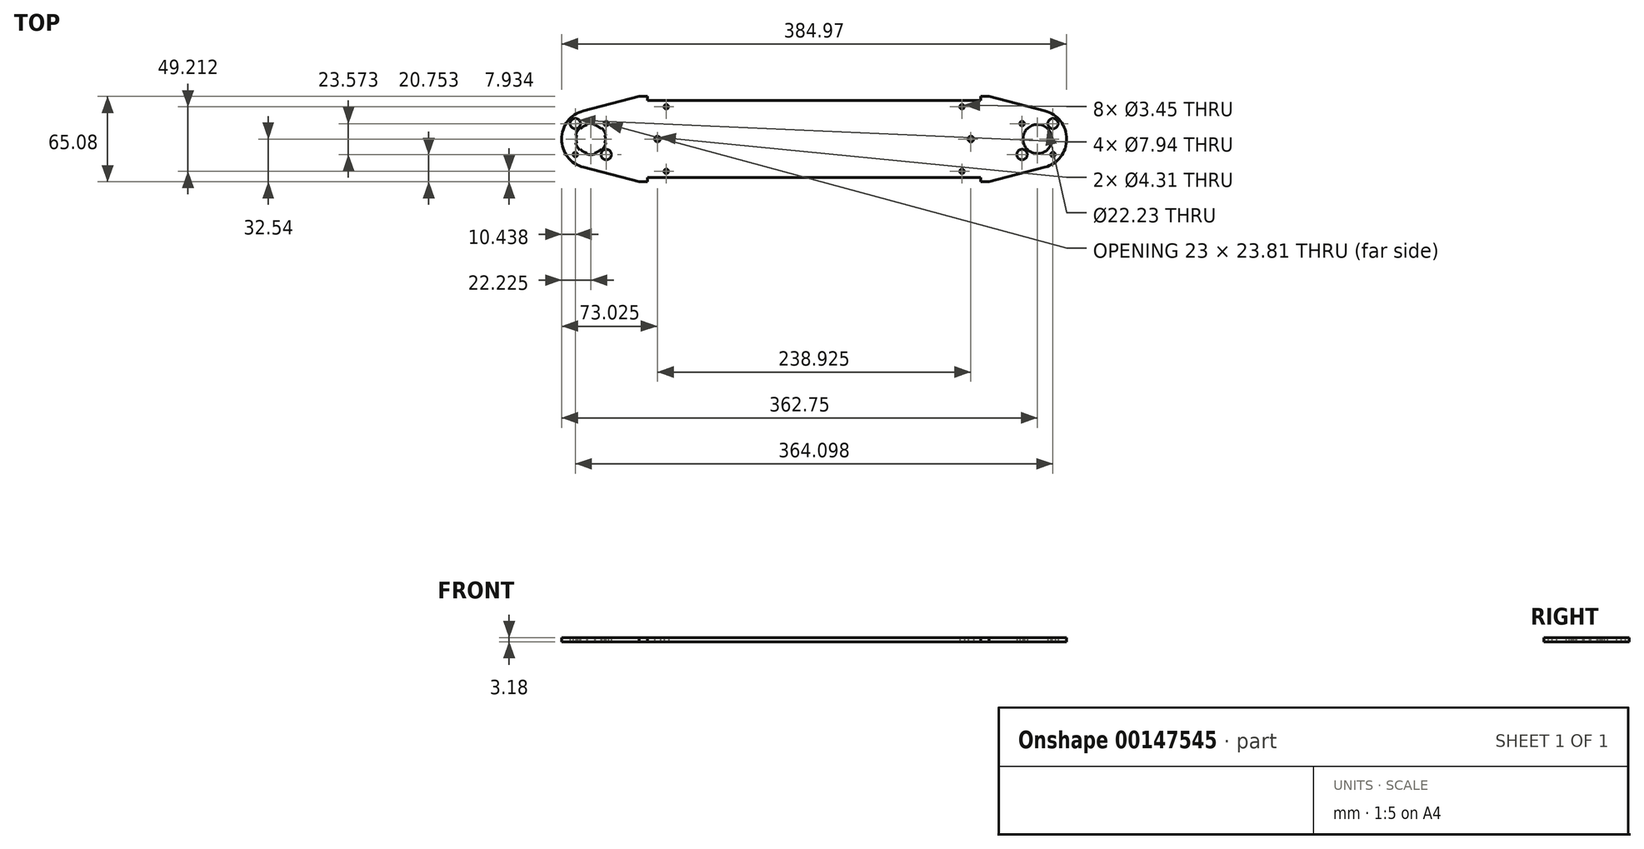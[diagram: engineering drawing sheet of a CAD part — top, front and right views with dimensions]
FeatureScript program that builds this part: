
annotation { "Feature Type Name" : "Feature", "Feature Type Description" : "" }
export const myFeature = defineFeature(function(context is Context, id is Id, definition is map)
    precondition{}
    {
        {
            var Q0;
            Q0=qCreatedBy(makeId("Top.planeOp"),FACE);
            var sketch = newSketch(context, id + "F0", { "sketchPlane" : qUnion([Q0])});
            skPoint(sketch, "E0.rect.middle", {"position": v(0, 0) * mm});
            skCircle(sketch, "E1", {"center": v(0, 0) * mm, "radius": 11.11 * mm});
            skLineSegment(sketch, "E2.bottom", {"start": v(11.79, 11.79) * mm, "end": v(-11.79, 11.79) * mm, "construction": true});
            skLineSegment(sketch, "E2.left", {"start": v(11.79, 11.79) * mm, "end": v(11.79, -11.79) * mm, "construction": true});
            skLineSegment(sketch, "E2.right", {"start": v(-11.79, 11.79) * mm, "end": v(-11.79, -11.79) * mm, "construction": true});
            skCircle(sketch, "E3", {"center": v(11.79, 11.79) * mm, "radius": 5.56 * mm, "construction": true});
            skCircle(sketch, "E4", {"center": v(-11.79, 11.79) * mm, "radius": 1.73 * mm});
            skCircle(sketch, "E5", {"center": v(11.79, 11.79) * mm, "radius": 3.97 * mm});
            skCircle(sketch, "E6", {"center": v(11.79, -11.79) * mm, "radius": 1.73 * mm});
            skCircle(sketch, "E7", {"center": v(-11.79, -11.79) * mm, "radius": 3.97 * mm});
            skArc(sketch, "E8", {"start": v(-346.1, 21.51) * mm, "mid": v(-362.75, 0) * mm, "end": v(-346.1, -21.51) * mm});
            skLineSegment(sketch, "E9.bottom", {"start": v(-352.31, 11.79) * mm, "end": v(-328.74, 11.79) * mm, "construction": true});
            skLineSegment(sketch, "E9.top", {"start": v(-352.31, -11.79) * mm, "end": v(-328.74, -11.79) * mm, "construction": true});
            skLineSegment(sketch, "E9.left", {"start": v(-352.31, 11.79) * mm, "end": v(-352.31, -11.79) * mm, "construction": true});
            skLineSegment(sketch, "E9.right", {"start": v(-328.74, 11.79) * mm, "end": v(-328.74, -11.79) * mm, "construction": true});
            skCircle(sketch, "E10", {"center": v(-328.74, 11.79) * mm, "radius": 1.73 * mm});
            skCircle(sketch, "E11", {"center": v(-340.53, 0) * mm, "radius": 11.11 * mm});
            skCircle(sketch, "E12", {"center": v(-352.31, 11.79) * mm, "radius": 3.97 * mm});
            skCircle(sketch, "E13", {"center": v(-352.31, -11.79) * mm, "radius": 1.73 * mm});
            skCircle(sketch, "E14", {"center": v(-328.74, -11.79) * mm, "radius": 3.97 * mm});
            skLineSegment(sketch, "E15", {"start": v(0, 0) * mm, "end": v(-340.53, 0) * mm, "construction": true});
            skLineSegment(sketch, "E16", {"start": v(-346.1, -21.51) * mm, "end": v(-303.61, -32.54) * mm});
            skLineSegment(sketch, "E17", {"start": v(-346.1, 21.51) * mm, "end": v(-303.61, 32.54) * mm});
            skLineSegment(sketch, "E18", {"start": v(-297.26, -29.37) * mm, "end": v(-43.26, -29.37) * mm});
            skLineSegment(sketch, "E19", {"start": v(-297.26, 29.37) * mm, "end": v(-43.26, 29.37) * mm});
            skLineSegment(sketch, "E20", {"start": v(-297.26, 32.54) * mm, "end": v(-297.26, 29.37) * mm});
            skLineSegment(sketch, "E21", {"start": v(-297.26, 32.54) * mm, "end": v(-303.61, 32.54) * mm});
            skLineSegment(sketch, "E22", {"start": v(-297.26, -29.37) * mm, "end": v(-297.26, -32.54) * mm});
            skLineSegment(sketch, "E23", {"start": v(-297.26, -32.54) * mm, "end": v(-303.61, -32.54) * mm});
            skLineSegment(sketch, "E24", {"start": v(-43.26, -29.37) * mm, "end": v(-43.26, -32.54) * mm});
            skLineSegment(sketch, "E25", {"start": v(-43.26, -32.54) * mm, "end": v(-36.91, -32.54) * mm});
            skLineSegment(sketch, "E26", {"start": v(-43.26, 29.37) * mm, "end": v(-43.26, 32.54) * mm});
            skLineSegment(sketch, "E27", {"start": v(-43.26, 32.54) * mm, "end": v(-36.91, 32.54) * mm});
            skLineSegment(sketch, "E28", {"start": v(-36.91, -32.54) * mm, "end": v(5.58, -21.51) * mm});
            skLineSegment(sketch, "E29", {"start": v(5.58, 21.51) * mm, "end": v(-36.91, 32.54) * mm});
            skArc(sketch, "E30", {"start": v(5.58, -21.51) * mm, "mid": v(22.23, 0) * mm, "end": v(5.58, 21.51) * mm});
            skLineSegment(sketch, "E31", {"start": v(-297.26, 29.37) * mm, "end": v(-297.26, 24.6) * mm, "construction": true});
            skLineSegment(sketch, "E32", {"start": v(-297.26, 24.6) * mm, "end": v(-282.98, 24.6) * mm, "construction": true});
            skLineSegment(sketch, "E33", {"start": v(-297.26, -29.37) * mm, "end": v(-297.26, -24.6) * mm, "construction": true});
            skLineSegment(sketch, "E34", {"start": v(-297.26, -24.6) * mm, "end": v(-282.98, -24.6) * mm, "construction": true});
            skLineSegment(sketch, "E35", {"start": v(-43.26, -29.37) * mm, "end": v(-43.26, -24.6) * mm, "construction": true});
            skLineSegment(sketch, "E36", {"start": v(-43.26, -24.6) * mm, "end": v(-57.55, -24.6) * mm, "construction": true});
            skLineSegment(sketch, "E37", {"start": v(-43.26, 29.37) * mm, "end": v(-43.26, 24.6) * mm, "construction": true});
            skLineSegment(sketch, "E38", {"start": v(-43.26, 24.6) * mm, "end": v(-57.55, 24.6) * mm, "construction": true});
            skCircle(sketch, "E39", {"center": v(-282.98, 24.6) * mm, "radius": 1.73 * mm});
            skCircle(sketch, "E40", {"center": v(-57.55, 24.6) * mm, "radius": 1.73 * mm});
            skCircle(sketch, "E41", {"center": v(-57.55, -24.6) * mm, "radius": 1.73 * mm});
            skCircle(sketch, "E42", {"center": v(-282.98, -24.6) * mm, "radius": 1.73 * mm});
            skLineSegment(sketch, "E43", {"start": v(-11.79, -11.79) * mm, "end": v(11.79, -11.79) * mm, "construction": true});
            skLineSegment(sketch, "E44", {"start": v(-170.26, -29.37) * mm, "end": v(-170.26, 0) * mm, "construction": true});
            skLineSegment(sketch, "E45", {"start": v(-170.26, 0) * mm, "end": v(-170.26, 29.37) * mm, "construction": true});
            skLineSegment(sketch, "E46", {"start": v(-328.74, 11.79) * mm, "end": v(-289.73, 11.79) * mm, "construction": true});
            skLineSegment(sketch, "E47", {"start": v(-289.73, 11.79) * mm, "end": v(-289.73, 0) * mm, "construction": true});
            skLineSegment(sketch, "E48", {"start": v(-11.79, 11.79) * mm, "end": v(-50.8, 11.79) * mm, "construction": true});
            skLineSegment(sketch, "E49", {"start": v(-50.8, 11.79) * mm, "end": v(-50.8, 0) * mm, "construction": true});
            skCircle(sketch, "E50", {"center": v(-50.8, 0) * mm, "radius": 2.15 * mm});
            skCircle(sketch, "E51", {"center": v(-289.73, 0) * mm, "radius": 2.15 * mm});
            skSolve(sketch);
        }
        {
            var Q0;
            Q0=qSketchRegion(id+"F0",true);
            extrude(context, id + "F1", {"entities" : qUnion([Q0]), "depth" : 3.17 * mm});
        }
        {
            var Q0;
            Q0=makeQuery(id+"F1.opExtrude","CAP_FACE",FACE,{"disambiguationData":[OSD([sQuery(id+"F0.wireOp",EDGE,"d63eafa0-1946-4b0e-8293-95e246b273c5.rect.bottom"),sQuery(id+"F0.wireOp",EDGE,"d63eafa0-1946-4b0e-8293-95e246b273c5.rect.top"),sQuery(id+"F0.wireOp",EDGE,"5983dcdd-59a7-4b72-80fd-e4567be1ae8a"),sQuery(id+"F0.wireOp",EDGE,"5a538b3e-fc2b-4d64-affd-5d60433388e5"),sQuery(id+"F0.wireOp",EDGE,"72e86de7-b207-474f-aadf-64543fae3f9b"),sQuery(id+"F0.wireOp",EDGE,"1c038800-5bd5-4753-8b38-6da13ef78ef9"),sQuery(id+"F0.wireOp",EDGE,"EbMUZoU6-Ffds-1dNq-SxhE-hPi8oSjhvaod"),sQuery(id+"F0.wireOp",EDGE,"RfgQjzcw-1Izs-lnTa-bWkk-oBHRDQjbZqQC"),sQuery(id+"F0.wireOp",EDGE,"1cCQAcjj-TyQA-3DMx-kDix-v5yZVaaGeXVM"),sQuery(id+"F0.wireOp",EDGE,"7KPu8lni-3ZWA-t6oJ-FRoh-C5MB3aVr7E9B"),sQuery(id+"F0.wireOp",EDGE,"bSzr06ES-7M0i-Fw5H-UJmt-4e4EQGRPIe4n"),sQuery(id+"F0.wireOp",EDGE,"WGsr6OjU-OX8l-mawA-7cCc-MfOuMOY06Cp5"),sQuery(id+"F0.wireOp",EDGE,"9mrz1cDN-18gM-20ra-6VCO-jp25g10tvNn2"),sQuery(id+"F0.wireOp",EDGE,"G0uOisy3-Mq6h-PcKh-Zkf4-CVoCvP3Hii1l"),sQuery(id+"F0.wireOp",EDGE,"1ae556be-0ab9-4322-b48e-98cf5a741ae0"),sQuery(id+"F0.wireOp",EDGE,"676cd913-43f8-42b3-8cdc-a90136d19ef5"),sQuery(id+"F0.wireOp",EDGE,"xnt2EyF8-ZVyQ-RbWD-GIsP-ThkcyX8ZioIH.bottom"),sQuery(id+"F0.wireOp",EDGE,"xnt2EyF8-ZVyQ-RbWD-GIsP-ThkcyX8ZioIH.top"),sQuery(id+"F0.wireOp",EDGE,"xnt2EyF8-ZVyQ-RbWD-GIsP-ThkcyX8ZioIH.left"),sQuery(id+"F0.wireOp",EDGE,"E1"),sQuery(id+"F0.wireOp",EDGE,"Jo9pZc7T-t0kF-vjz1-dNbX-L65bwNqtrrdz"),sQuery(id+"F0.wireOp",EDGE,"lEYoY9t7-PMOS-SVp6-xfnB-Xp9WdWMCDdum"),sQuery(id+"F0.wireOp",EDGE,"s7aM02SC-9XQ7-dueL-DqMg-ZFuJqOofj9mt"),sQuery(id+"F0.wireOp",EDGE,"deKa9ngt-XMq2-GGkr-SZIa-KlyN0U5bcCDe"),sQuery(id+"F0.wireOp",EDGE,"E4"),sQuery(id+"F0.wireOp",EDGE,"E5"),sQuery(id+"F0.wireOp",EDGE,"E6"),sQuery(id+"F0.wireOp",EDGE,"E7"),sQuery(id+"F0.wireOp",EDGE,"E8"),sQuery(id+"F0.wireOp",EDGE,"E10"),sQuery(id+"F0.wireOp",EDGE,"E11"),sQuery(id+"F0.wireOp",EDGE,"E12"),sQuery(id+"F0.wireOp",EDGE,"E13"),sQuery(id+"F0.wireOp",EDGE,"E14")])],"isStart":true});
            var sketch = newSketch(context, id + "F2", { "sketchPlane" : qUnion([Q0])});
            skLineSegment(sketch, "E52", {"start": v(-340.53, 0) * mm, "end": v(-350.15, -5.56) * mm, "construction": true});
            skArc(sketch, "E53", {"start": v(-351.26, -2.88) * mm, "mid": v(-350.15, -5.56) * mm, "end": v(-348.38, -7.86) * mm});
            skLineSegment(sketch, "E54", {"start": v(-340.53, 0) * mm, "end": v(-348.38, -7.86) * mm, "construction": true});
            skLineSegment(sketch, "E55", {"start": v(-340.53, 0) * mm, "end": v(-351.26, -2.88) * mm, "construction": true});
            skLineSegment(sketch, "E56", {"start": v(-348.38, -7.86) * mm, "end": v(-348.94, -8.42) * mm});
            skLineSegment(sketch, "E57", {"start": v(-351.26, -2.88) * mm, "end": v(-352.03, -3.08) * mm});
            skArc(sketch, "E58", {"start": v(-352.03, -3.08) * mm, "mid": v(-350.84, -5.95) * mm, "end": v(-348.94, -8.42) * mm});
            skLineSegment(sketch, "E59", {"start": v(-340.53, 0) * mm, "end": v(-351.64, 0) * mm, "construction": true});
            skSolve(sketch);
        }
        {
            var Q0;
            Q0=qSketchRegion(id+"F2",true);
            var Q1;
            Q1=makeQuery(id+"F1.opExtrude","CAP_FACE",FACE,{"disambiguationData":[OSD([sQuery(id+"F0.wireOp",EDGE,"d63eafa0-1946-4b0e-8293-95e246b273c5.rect.bottom"),sQuery(id+"F0.wireOp",EDGE,"d63eafa0-1946-4b0e-8293-95e246b273c5.rect.top"),sQuery(id+"F0.wireOp",EDGE,"5983dcdd-59a7-4b72-80fd-e4567be1ae8a"),sQuery(id+"F0.wireOp",EDGE,"5a538b3e-fc2b-4d64-affd-5d60433388e5"),sQuery(id+"F0.wireOp",EDGE,"72e86de7-b207-474f-aadf-64543fae3f9b"),sQuery(id+"F0.wireOp",EDGE,"1c038800-5bd5-4753-8b38-6da13ef78ef9"),sQuery(id+"F0.wireOp",EDGE,"EbMUZoU6-Ffds-1dNq-SxhE-hPi8oSjhvaod"),sQuery(id+"F0.wireOp",EDGE,"RfgQjzcw-1Izs-lnTa-bWkk-oBHRDQjbZqQC"),sQuery(id+"F0.wireOp",EDGE,"1cCQAcjj-TyQA-3DMx-kDix-v5yZVaaGeXVM"),sQuery(id+"F0.wireOp",EDGE,"7KPu8lni-3ZWA-t6oJ-FRoh-C5MB3aVr7E9B"),sQuery(id+"F0.wireOp",EDGE,"bSzr06ES-7M0i-Fw5H-UJmt-4e4EQGRPIe4n"),sQuery(id+"F0.wireOp",EDGE,"WGsr6OjU-OX8l-mawA-7cCc-MfOuMOY06Cp5"),sQuery(id+"F0.wireOp",EDGE,"9mrz1cDN-18gM-20ra-6VCO-jp25g10tvNn2"),sQuery(id+"F0.wireOp",EDGE,"G0uOisy3-Mq6h-PcKh-Zkf4-CVoCvP3Hii1l"),sQuery(id+"F0.wireOp",EDGE,"1ae556be-0ab9-4322-b48e-98cf5a741ae0"),sQuery(id+"F0.wireOp",EDGE,"676cd913-43f8-42b3-8cdc-a90136d19ef5"),sQuery(id+"F0.wireOp",EDGE,"xnt2EyF8-ZVyQ-RbWD-GIsP-ThkcyX8ZioIH.bottom"),sQuery(id+"F0.wireOp",EDGE,"xnt2EyF8-ZVyQ-RbWD-GIsP-ThkcyX8ZioIH.top"),sQuery(id+"F0.wireOp",EDGE,"xnt2EyF8-ZVyQ-RbWD-GIsP-ThkcyX8ZioIH.left"),sQuery(id+"F0.wireOp",EDGE,"E1"),sQuery(id+"F0.wireOp",EDGE,"Jo9pZc7T-t0kF-vjz1-dNbX-L65bwNqtrrdz"),sQuery(id+"F0.wireOp",EDGE,"lEYoY9t7-PMOS-SVp6-xfnB-Xp9WdWMCDdum"),sQuery(id+"F0.wireOp",EDGE,"s7aM02SC-9XQ7-dueL-DqMg-ZFuJqOofj9mt"),sQuery(id+"F0.wireOp",EDGE,"deKa9ngt-XMq2-GGkr-SZIa-KlyN0U5bcCDe"),sQuery(id+"F0.wireOp",EDGE,"E4"),sQuery(id+"F0.wireOp",EDGE,"E5"),sQuery(id+"F0.wireOp",EDGE,"E6"),sQuery(id+"F0.wireOp",EDGE,"E7"),sQuery(id+"F0.wireOp",EDGE,"E8"),sQuery(id+"F0.wireOp",EDGE,"E10"),sQuery(id+"F0.wireOp",EDGE,"E11"),sQuery(id+"F0.wireOp",EDGE,"E12"),sQuery(id+"F0.wireOp",EDGE,"E13"),sQuery(id+"F0.wireOp",EDGE,"E14")])],"isStart":false});
            extrude(context, id + "F3", {"entities" : qUnion([Q0]), "operationType" : NewBodyOperationType.REMOVE, "endBound" : BoundingType.UP_TO_SURFACE, "oppositeDirection" : true, "endBoundEntityFace" : qUnion([Q1]), "depth" : 25.4 * mm});
        }
        {
            var Q0;
            Q0=makeQuery(id+"F3.boolean.opBoolean","COPY",FACE,{"derivedFrom":makeQuery(id+"F3.opExtrude","SWEPT_FACE",FACE,{"disambiguationData":[OSD([sQuery(id+"F2.wireOp",EDGE,"E56")])]})});
            var Q1;
            Q1=makeQuery(id+"F3.boolean.opBoolean","COPY",FACE,{"derivedFrom":makeQuery(id+"F3.opExtrude","SWEPT_FACE",FACE,{"disambiguationData":[OSD([sQuery(id+"F2.wireOp",EDGE,"E58")])]})});
            var Q2;
            Q2=makeQuery(id+"F3.boolean.opBoolean","COPY",FACE,{"derivedFrom":makeQuery(id+"F3.opExtrude","SWEPT_FACE",FACE,{"disambiguationData":[OSD([sQuery(id+"F2.wireOp",EDGE,"E57")])]})});
            var Q3;
            Q3=makeQuery(id+"F1.opExtrude","SWEPT_FACE",FACE,{"disambiguationData":[OSD([sQuery(id+"F0.wireOp",EDGE,"E11")])]});
            circularPattern(context, id + "F4", {"patternType" : PatternType.FACE, "faces" : qUnion([Q0, Q1, Q2]), "axis" : qUnion([Q3]), "angle" : 60 * degree, "instanceCount" : 6});
        }
    });
